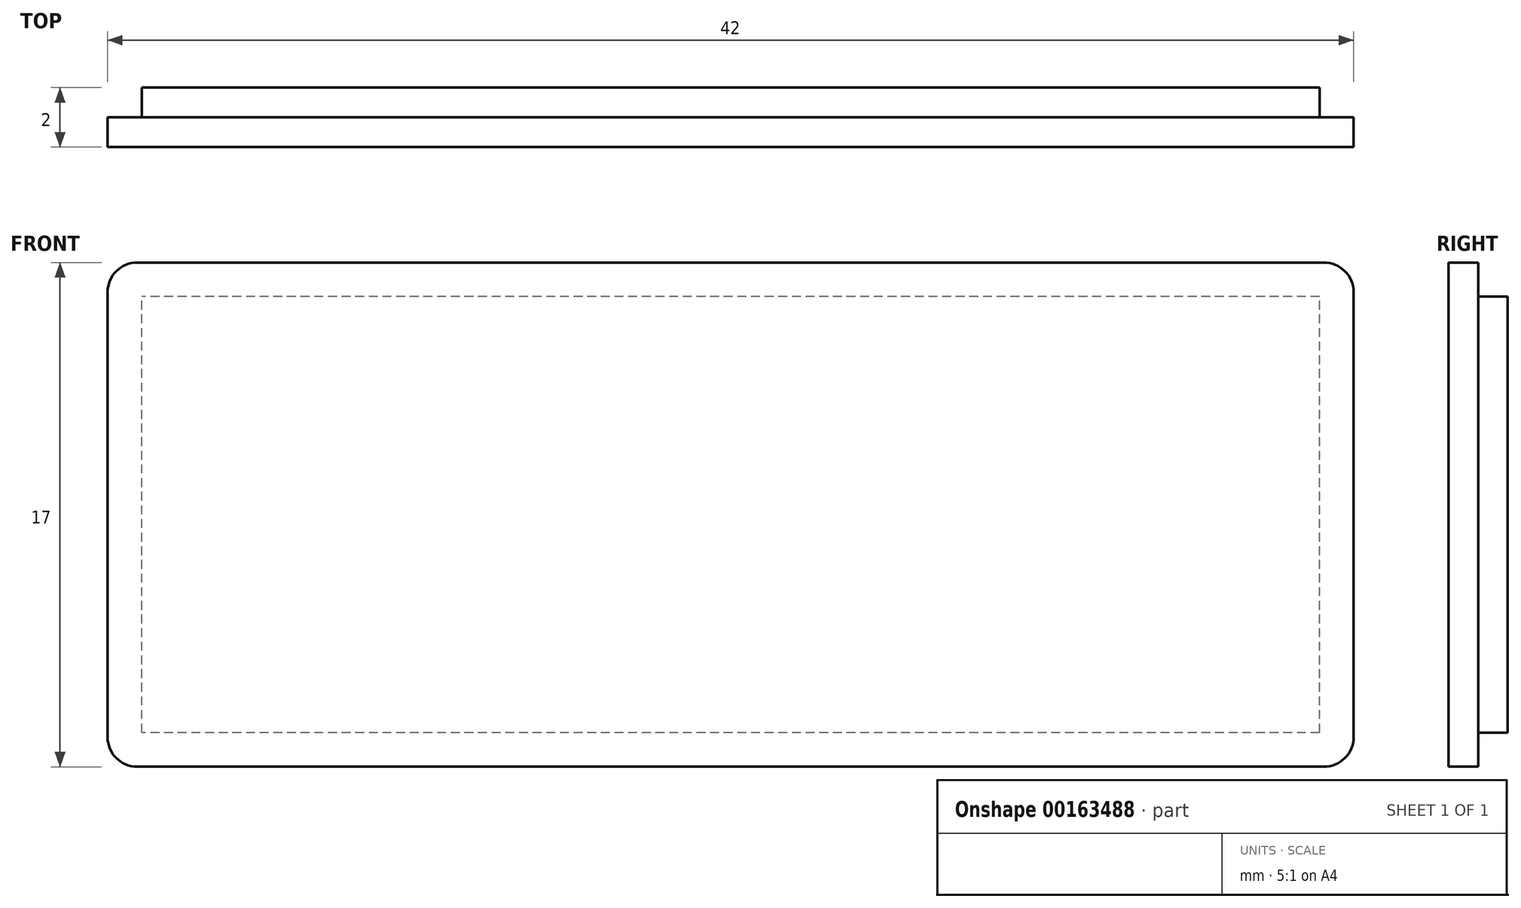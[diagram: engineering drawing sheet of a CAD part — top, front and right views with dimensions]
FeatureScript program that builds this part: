
annotation { "Feature Type Name" : "Feature", "Feature Type Description" : "" }
export const myFeature = defineFeature(function(context is Context, id is Id, definition is map)
    precondition{}
    {
        {
            var Q0;
            Q0=qCreatedBy(makeId("Front.planeOp"),FACE);
            var sketch = newSketch(context, id + "F0", { "sketchPlane" : qUnion([Q0])});
            skLineSegment(sketch, "E0.bottom", {"start": v(20.26, -7.08) * mm, "end": v(-19.44, -7.08) * mm});
            skLineSegment(sketch, "E0.top", {"start": v(20.26, 7.62) * mm, "end": v(-19.44, 7.62) * mm});
            skLineSegment(sketch, "E0.left", {"start": v(20.26, -7.08) * mm, "end": v(20.26, 7.62) * mm});
            skLineSegment(sketch, "E0.right", {"start": v(-19.44, -7.08) * mm, "end": v(-19.44, 7.62) * mm});
            skPoint(sketch, "E0.middle", {"position": v(0.41, 0.27) * mm});
            skLineSegment(sketch, "E1.bottom", {"start": v(20.41, -8.23) * mm, "end": v(-19.59, -8.23) * mm});
            skLineSegment(sketch, "E1.top", {"start": v(20.41, 8.77) * mm, "end": v(-19.59, 8.77) * mm});
            skLineSegment(sketch, "E1.left", {"start": v(21.41, -7.23) * mm, "end": v(21.41, 7.77) * mm});
            skLineSegment(sketch, "E1.right", {"start": v(-20.59, -7.23) * mm, "end": v(-20.59, 7.77) * mm});
            skPoint(sketch, "E2.visualSharp", {"position": v(-20.59, 8.77) * mm});
            skArc(sketch, "E2.filletArc", {"start": v(-19.59, 8.77) * mm, "mid": v(-20.3, 8.48) * mm, "end": v(-20.59, 7.77) * mm});
            skPoint(sketch, "E3.visualSharp", {"position": v(-20.59, -8.23) * mm});
            skArc(sketch, "E3.filletArc", {"start": v(-20.59, -7.23) * mm, "mid": v(-20.3, -7.93) * mm, "end": v(-19.59, -8.23) * mm});
            skPoint(sketch, "E4.visualSharp", {"position": v(21.41, -8.23) * mm});
            skArc(sketch, "E4.filletArc", {"start": v(20.41, -8.23) * mm, "mid": v(21.12, -7.93) * mm, "end": v(21.41, -7.23) * mm});
            skPoint(sketch, "E5.visualSharp", {"position": v(21.41, 8.77) * mm});
            skArc(sketch, "E5.filletArc", {"start": v(21.41, 7.77) * mm, "mid": v(21.12, 8.48) * mm, "end": v(20.41, 8.77) * mm});
            skSolve(sketch);
        }
        {
            var Q0;
            Q0=makeQuery(id+"F0.imprint","IMPRINT",FACE,{"disambiguationData":[TD([[makeQuery(id+"F0.imprint","IMPRINT",EDGE,{"derivedFrom":sQuery(id+"F0.wireOp",EDGE,"E0.bottom")}),-1.0]])]});
            var Q1;
            Q1=makeQuery(id+"F0.imprint","IMPRINT",FACE,{"disambiguationData":[TD([[makeQuery(id+"F0.imprint","IMPRINT",EDGE,{"derivedFrom":sQuery(id+"F0.wireOp",EDGE,"E0.bottom")}),1.0]])]});
            extrude(context, id + "F1", {"entities" : qUnion([Q0, Q1]), "depth" : 1 * mm});
        }
        {
            var Q0;
            Q0=makeQuery(id+"F0.imprint","IMPRINT",FACE,{"disambiguationData":[TD([[makeQuery(id+"F0.imprint","IMPRINT",EDGE,{"derivedFrom":sQuery(id+"F0.wireOp",EDGE,"E0.bottom")}),-1.0]])]});
            extrude(context, id + "F2", {"entities" : qUnion([Q0]), "operationType" : NewBodyOperationType.ADD, "oppositeDirection" : true, "depth" : 1 * mm});
        }
    });
